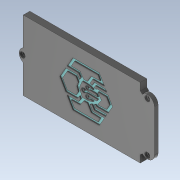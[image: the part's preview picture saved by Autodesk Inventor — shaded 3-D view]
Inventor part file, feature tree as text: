
AUTODESK INVENTOR PART (.ipt)
format: ipt  version: 2020 (Build 240168000, 168)  size: 526,336 bytes
history: native  units: mm
features: reference x9, extrude x4, sketch x4, other x3, projected_geometry x1
ambient origin geometry x8: Origin, YZ Plane, XZ Plane, XY Plane, X Axis, Y Axis, Z Axis, Center Point
bodies: Solid1 (feature_tree)
feature tree (21):
  extrude  "Extrusion1"  Depth=4.0mm TaperAngle=0.0deg
  extrude  "Extrusion2"  Depth=5.6mm
  extrude  "Extrusion3"  Depth=2.0mm TaperAngle=0.0deg
  extrude  "Extrusion5"  Depth=1.0mm
  sketch  "Sketch1"  dims[d0=4.0mm d1=0.0mm d2=7.0mm d3=0.0mm]
  reference  "Reference1"
  reference  "Reference2"
  reference  "Reference3"
  reference  "Reference4"
  reference  "Reference5"
  reference  "Reference6"
  sketch  "Sketch2"  dims[d4=5.6mm d5=5.6mm]
  reference  "Reference7"
  reference  "Reference8"
  reference  "Reference9"
  sketch  "Sketch3"  dims[d6=5.6mm d7=2.0mm d8=0.0mm]
  projected_geometry  "Projected Loop1"
  sketch  "Sketch6"  dims[d457=1.0mm d458=0.0mm d459=0.5mm d460=0.872665mm d461=0.5mm d462=0.872665mm]
  parser-record x1  (decoder bookkeeping rows leaked as tree rows — omitted from the tree; the rows remain in map.json)
  other  "Assembly1.iam"
  other  "BodyBot:1"
note: 1 file-system path scrubbed to <path> (originals preserved in map.json)
